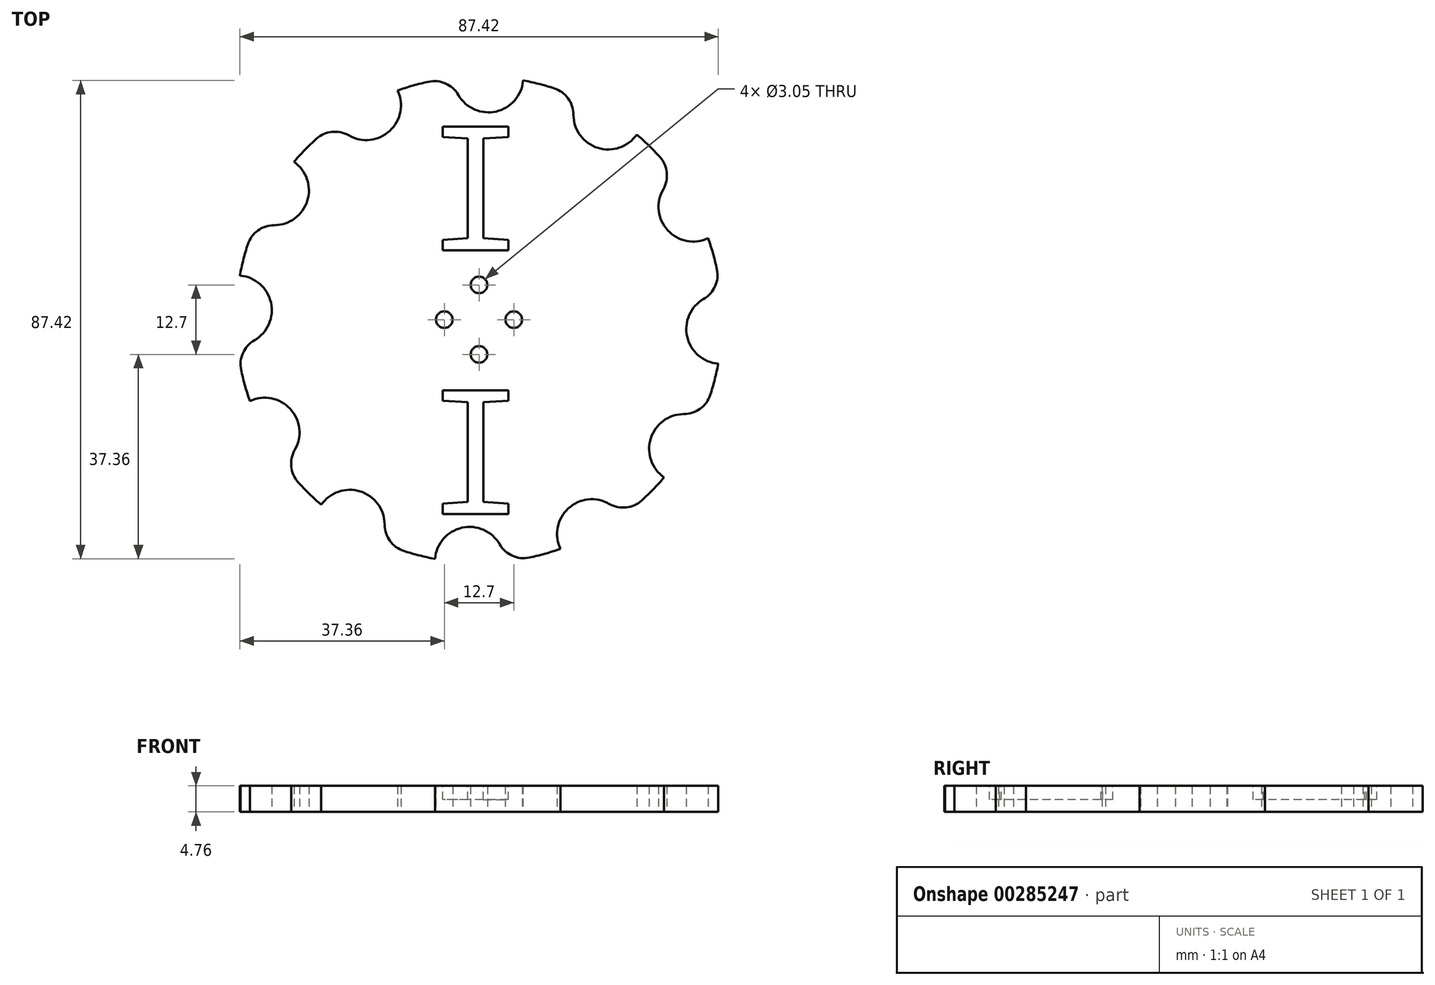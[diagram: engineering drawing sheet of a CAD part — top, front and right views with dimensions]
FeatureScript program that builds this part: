
annotation { "Feature Type Name" : "Feature", "Feature Type Description" : "" }
export const myFeature = defineFeature(function(context is Context, id is Id, definition is map)
    precondition{}
    {
        {
            var Q0;
            Q0=qCreatedBy(makeId("Top.planeOp"),FACE);
            var sketch = newSketch(context, id + "F0", { "sketchPlane" : qUnion([Q0])});
            skArc(sketch, "E0", {"start": v(-9.23, 43.48) * mm, "mid": v(-12.08, 42.78) * mm, "end": v(-14.88, 41.89) * mm});
            skCircle(sketch, "E1", {"center": v(0, 0) * mm, "radius": 6.35 * mm, "construction": true});
            skCircle(sketch, "E2", {"center": v(0, 6.35) * mm, "radius": 1.52 * mm});
            skCircle(sketch, "E3", {"center": v(-6.35, 0) * mm, "radius": 1.52 * mm});
            skCircle(sketch, "E4", {"center": v(0, -6.35) * mm, "radius": 1.52 * mm});
            skCircle(sketch, "E5", {"center": v(6.35, 0) * mm, "radius": 1.52 * mm});
            skArc(sketch, "E6", {"start": v(-3.77, 41.05) * mm, "mid": v(3.12, 38.03) * mm, "end": v(8.06, 43.71) * mm});
            skArc(sketch, "E7.1.0", {"start": v(-23.8, 33.67) * mm, "mid": v(-16.32, 34.5) * mm, "end": v(-14.88, 41.89) * mm});
            skArc(sketch, "E7.2.0", {"start": v(-37.44, 17.26) * mm, "mid": v(-31.38, 21.72) * mm, "end": v(-33.83, 28.83) * mm});
            skArc(sketch, "E7.3.0", {"start": v(-41.05, -3.77) * mm, "mid": v(-38.03, 3.12) * mm, "end": v(-43.71, 8.06) * mm});
            skArc(sketch, "E7.4.0", {"start": v(-33.67, -23.8) * mm, "mid": v(-34.5, -16.32) * mm, "end": v(-41.89, -14.88) * mm});
            skArc(sketch, "E7.5.0", {"start": v(-17.26, -37.44) * mm, "mid": v(-21.72, -31.38) * mm, "end": v(-28.83, -33.83) * mm});
            skArc(sketch, "E7.6.0", {"start": v(3.77, -41.05) * mm, "mid": v(-3.12, -38.03) * mm, "end": v(-8.06, -43.71) * mm});
            skArc(sketch, "E7.7.0", {"start": v(23.8, -33.67) * mm, "mid": v(16.32, -34.5) * mm, "end": v(14.88, -41.89) * mm});
            skArc(sketch, "E7.8.0", {"start": v(37.44, -17.26) * mm, "mid": v(31.38, -21.72) * mm, "end": v(33.83, -28.83) * mm});
            skArc(sketch, "E7.9.0", {"start": v(41.05, 3.77) * mm, "mid": v(38.03, -3.12) * mm, "end": v(43.71, -8.06) * mm});
            skArc(sketch, "E7.10.0", {"start": v(33.67, 23.8) * mm, "mid": v(34.5, 16.32) * mm, "end": v(41.89, 14.88) * mm});
            skArc(sketch, "E7.11.0", {"start": v(17.26, 37.44) * mm, "mid": v(21.72, 31.38) * mm, "end": v(28.83, 33.83) * mm});
            skArc(sketch, "E8.trimOffspring", {"start": v(13.75, 42.27) * mm, "mid": v(10.93, 43.09) * mm, "end": v(8.06, 43.71) * mm});
            skArc(sketch, "E9.trimOffspring", {"start": v(33.04, 29.73) * mm, "mid": v(31, 31.85) * mm, "end": v(28.83, 33.83) * mm});
            skArc(sketch, "E10.trimOffspring", {"start": v(43.48, 9.23) * mm, "mid": v(42.78, 12.08) * mm, "end": v(41.89, 14.88) * mm});
            skArc(sketch, "E11.trimOffspring", {"start": v(42.27, -13.75) * mm, "mid": v(43.09, -10.93) * mm, "end": v(43.71, -8.06) * mm});
            skArc(sketch, "E12.trimOffspring", {"start": v(29.73, -33.04) * mm, "mid": v(31.85, -31) * mm, "end": v(33.83, -28.83) * mm});
            skArc(sketch, "E13.trimOffspring", {"start": v(9.23, -43.48) * mm, "mid": v(12.08, -42.78) * mm, "end": v(14.88, -41.89) * mm});
            skArc(sketch, "E14.trimOffspring", {"start": v(-13.75, -42.27) * mm, "mid": v(-10.93, -43.09) * mm, "end": v(-8.06, -43.71) * mm});
            skArc(sketch, "E15.trimOffspring", {"start": v(-33.04, -29.73) * mm, "mid": v(-31, -31.85) * mm, "end": v(-28.83, -33.83) * mm});
            skArc(sketch, "E16.trimOffspring", {"start": v(-43.48, -9.23) * mm, "mid": v(-42.78, -12.08) * mm, "end": v(-41.89, -14.88) * mm});
            skArc(sketch, "E17.trimOffspring", {"start": v(-42.27, 13.75) * mm, "mid": v(-43.09, 10.93) * mm, "end": v(-43.71, 8.06) * mm});
            skArc(sketch, "E18.trimOffspring", {"start": v(-29.73, 33.04) * mm, "mid": v(-31.85, 31) * mm, "end": v(-33.83, 28.83) * mm});
            skPoint(sketch, "E19.visualSharp", {"position": v(-26.1, 35.97) * mm});
            skArc(sketch, "E19.filletArc", {"start": v(-23.8, 33.67) * mm, "mid": v(-26.86, 34.32) * mm, "end": v(-29.73, 33.04) * mm});
            skPoint(sketch, "E20.visualSharp", {"position": v(-40.6, 18.1) * mm});
            skArc(sketch, "E20.filletArc", {"start": v(-37.44, 17.26) * mm, "mid": v(-40.42, 16.29) * mm, "end": v(-42.27, 13.75) * mm});
            skPoint(sketch, "E21.visualSharp", {"position": v(-44.2, -4.62) * mm});
            skArc(sketch, "E21.filletArc", {"start": v(-41.05, -3.77) * mm, "mid": v(-43.15, -6.1) * mm, "end": v(-43.48, -9.23) * mm});
            skPoint(sketch, "E22.visualSharp", {"position": v(-35.97, -26.1) * mm});
            skArc(sketch, "E22.filletArc", {"start": v(-33.67, -23.8) * mm, "mid": v(-34.32, -26.86) * mm, "end": v(-33.04, -29.73) * mm});
            skPoint(sketch, "E23.visualSharp", {"position": v(-18.1, -40.6) * mm});
            skArc(sketch, "E23.filletArc", {"start": v(-17.26, -37.44) * mm, "mid": v(-16.29, -40.42) * mm, "end": v(-13.75, -42.27) * mm});
            skPoint(sketch, "E24.visualSharp", {"position": v(4.62, -44.2) * mm});
            skArc(sketch, "E24.filletArc", {"start": v(3.77, -41.05) * mm, "mid": v(6.1, -43.15) * mm, "end": v(9.23, -43.48) * mm});
            skPoint(sketch, "E25.visualSharp", {"position": v(26.1, -35.97) * mm});
            skArc(sketch, "E25.filletArc", {"start": v(23.8, -33.67) * mm, "mid": v(26.86, -34.32) * mm, "end": v(29.73, -33.04) * mm});
            skPoint(sketch, "E26.visualSharp", {"position": v(40.6, -18.1) * mm});
            skArc(sketch, "E26.filletArc", {"start": v(37.44, -17.26) * mm, "mid": v(40.42, -16.29) * mm, "end": v(42.27, -13.75) * mm});
            skPoint(sketch, "E27.visualSharp", {"position": v(44.2, 4.62) * mm});
            skArc(sketch, "E27.filletArc", {"start": v(41.05, 3.77) * mm, "mid": v(43.15, 6.1) * mm, "end": v(43.48, 9.23) * mm});
            skPoint(sketch, "E28.visualSharp", {"position": v(35.97, 26.1) * mm});
            skArc(sketch, "E28.filletArc", {"start": v(33.67, 23.8) * mm, "mid": v(34.32, 26.86) * mm, "end": v(33.04, 29.73) * mm});
            skPoint(sketch, "E29.visualSharp", {"position": v(18.1, 40.6) * mm});
            skArc(sketch, "E29.filletArc", {"start": v(17.26, 37.44) * mm, "mid": v(16.29, 40.42) * mm, "end": v(13.75, 42.27) * mm});
            skPoint(sketch, "E30.visualSharp", {"position": v(-4.62, 44.2) * mm});
            skArc(sketch, "E30.filletArc", {"start": v(-3.77, 41.05) * mm, "mid": v(-6.1, 43.15) * mm, "end": v(-9.23, 43.48) * mm});
            skSolve(sketch);
        }
        {
            var Q0;
            Q0=qSketchRegion(id+"F0",true);
            extrude(context, id + "F1", {"entities" : qUnion([Q0]), "depth" : 4.76 * mm});
        }
        {
            var Q0;
            Q0=makeQuery(id+"F1.opExtrude","CAP_FACE",FACE,{"disambiguationData":[OSD([sQuery(id+"F0.wireOp",EDGE,"E0"),sQuery(id+"F0.wireOp",EDGE,"E2"),sQuery(id+"F0.wireOp",EDGE,"E3"),sQuery(id+"F0.wireOp",EDGE,"E4"),sQuery(id+"F0.wireOp",EDGE,"E5"),sQuery(id+"F0.wireOp",EDGE,"E6"),sQuery(id+"F0.wireOp",EDGE,"E7.1.0"),sQuery(id+"F0.wireOp",EDGE,"E7.2.0"),sQuery(id+"F0.wireOp",EDGE,"E7.3.0"),sQuery(id+"F0.wireOp",EDGE,"E7.4.0"),sQuery(id+"F0.wireOp",EDGE,"E7.5.0"),sQuery(id+"F0.wireOp",EDGE,"E7.6.0"),sQuery(id+"F0.wireOp",EDGE,"E7.7.0"),sQuery(id+"F0.wireOp",EDGE,"E7.8.0"),sQuery(id+"F0.wireOp",EDGE,"E7.9.0"),sQuery(id+"F0.wireOp",EDGE,"E7.10.0"),sQuery(id+"F0.wireOp",EDGE,"E7.11.0"),sQuery(id+"F0.wireOp",EDGE,"E8.trimOffspring"),sQuery(id+"F0.wireOp",EDGE,"E9.trimOffspring"),sQuery(id+"F0.wireOp",EDGE,"E10.trimOffspring"),sQuery(id+"F0.wireOp",EDGE,"E11.trimOffspring"),sQuery(id+"F0.wireOp",EDGE,"E12.trimOffspring"),sQuery(id+"F0.wireOp",EDGE,"E13.trimOffspring"),sQuery(id+"F0.wireOp",EDGE,"E14.trimOffspring"),sQuery(id+"F0.wireOp",EDGE,"E15.trimOffspring"),sQuery(id+"F0.wireOp",EDGE,"E16.trimOffspring"),sQuery(id+"F0.wireOp",EDGE,"E17.trimOffspring"),sQuery(id+"F0.wireOp",EDGE,"E18.trimOffspring"),sQuery(id+"F0.wireOp",EDGE,"E19.filletArc"),sQuery(id+"F0.wireOp",EDGE,"E20.filletArc"),sQuery(id+"F0.wireOp",EDGE,"E21.filletArc"),sQuery(id+"F0.wireOp",EDGE,"E22.filletArc"),sQuery(id+"F0.wireOp",EDGE,"E23.filletArc"),sQuery(id+"F0.wireOp",EDGE,"E24.filletArc"),sQuery(id+"F0.wireOp",EDGE,"E25.filletArc"),sQuery(id+"F0.wireOp",EDGE,"E26.filletArc"),sQuery(id+"F0.wireOp",EDGE,"E27.filletArc"),sQuery(id+"F0.wireOp",EDGE,"E28.filletArc"),sQuery(id+"F0.wireOp",EDGE,"E29.filletArc"),sQuery(id+"F0.wireOp",EDGE,"E30.filletArc")])],"isStart":false});
            var sketch = newSketch(context, id + "F2", { "sketchPlane" : qUnion([Q0])});
            skText(sketch, "E31", { "text": "I", "fontName": "DroidSansMono.ttf"});
            const initialGuessF2  = {"E31": [-0.01012, 0.0127, 1, 0, 0.0228]};
            skSetInitialGuess(sketch, initialGuessF2);
            skSolve(sketch);
        }
        {
            var Q0;
            Q0=qSketchRegion(id+"F2",true);
            extrude(context, id + "F3", {"entities" : qUnion([Q0]), "operationType" : NewBodyOperationType.REMOVE, "oppositeDirection" : true, "depth" : 2.54 * mm});
        }
        {
            var Q0;
            Q0=makeQuery(id+"F1.opExtrude","CAP_FACE",FACE,{"disambiguationData":[OSD([sQuery(id+"F0.wireOp",EDGE,"E0"),sQuery(id+"F0.wireOp",EDGE,"E2"),sQuery(id+"F0.wireOp",EDGE,"E3"),sQuery(id+"F0.wireOp",EDGE,"E4"),sQuery(id+"F0.wireOp",EDGE,"E5"),sQuery(id+"F0.wireOp",EDGE,"E6"),sQuery(id+"F0.wireOp",EDGE,"E7.1.0"),sQuery(id+"F0.wireOp",EDGE,"E7.2.0"),sQuery(id+"F0.wireOp",EDGE,"E7.3.0"),sQuery(id+"F0.wireOp",EDGE,"E7.4.0"),sQuery(id+"F0.wireOp",EDGE,"E7.5.0"),sQuery(id+"F0.wireOp",EDGE,"E7.6.0"),sQuery(id+"F0.wireOp",EDGE,"E7.7.0"),sQuery(id+"F0.wireOp",EDGE,"E7.8.0"),sQuery(id+"F0.wireOp",EDGE,"E7.9.0"),sQuery(id+"F0.wireOp",EDGE,"E7.10.0"),sQuery(id+"F0.wireOp",EDGE,"E7.11.0"),sQuery(id+"F0.wireOp",EDGE,"E8.trimOffspring"),sQuery(id+"F0.wireOp",EDGE,"E9.trimOffspring"),sQuery(id+"F0.wireOp",EDGE,"E10.trimOffspring"),sQuery(id+"F0.wireOp",EDGE,"E11.trimOffspring"),sQuery(id+"F0.wireOp",EDGE,"E12.trimOffspring"),sQuery(id+"F0.wireOp",EDGE,"E13.trimOffspring"),sQuery(id+"F0.wireOp",EDGE,"E14.trimOffspring"),sQuery(id+"F0.wireOp",EDGE,"E15.trimOffspring"),sQuery(id+"F0.wireOp",EDGE,"E16.trimOffspring"),sQuery(id+"F0.wireOp",EDGE,"E17.trimOffspring"),sQuery(id+"F0.wireOp",EDGE,"E18.trimOffspring"),sQuery(id+"F0.wireOp",EDGE,"E19.filletArc"),sQuery(id+"F0.wireOp",EDGE,"E20.filletArc"),sQuery(id+"F0.wireOp",EDGE,"E21.filletArc"),sQuery(id+"F0.wireOp",EDGE,"E22.filletArc"),sQuery(id+"F0.wireOp",EDGE,"E23.filletArc"),sQuery(id+"F0.wireOp",EDGE,"E24.filletArc"),sQuery(id+"F0.wireOp",EDGE,"E25.filletArc"),sQuery(id+"F0.wireOp",EDGE,"E26.filletArc"),sQuery(id+"F0.wireOp",EDGE,"E27.filletArc"),sQuery(id+"F0.wireOp",EDGE,"E28.filletArc"),sQuery(id+"F0.wireOp",EDGE,"E29.filletArc"),sQuery(id+"F0.wireOp",EDGE,"E30.filletArc")])],"isStart":false});
            var sketch = newSketch(context, id + "F4", { "sketchPlane" : qUnion([Q0])});
            skSolve(sketch);
        }
        {
            var Q0;
            Q0=makeQuery(id+"F4.imprint","IMPRINT",FACE,{"disambiguationData":[TD([[makeQuery(id+"F4.imprint","IMPRINT",EDGE,{"derivedFrom":makeQuery(id+"F1.opExtrude","CAP_EDGE",EDGE,{"disambiguationData":[OSD([sQuery(id+"F0.wireOp",EDGE,"E0")])],"isStart":false})}),1.0]])]});
            var sketch = newSketch(context, id + "F5", { "sketchPlane" : qUnion([Q0])});
            skText(sketch, "E32", { "text": "I", "fontName": "DroidSansMono.ttf"});
            const initialGuessF5  = {"E32": [-0.01012, -0.0355, 1, 0, 0.0228]};
            skSetInitialGuess(sketch, initialGuessF5);
            skSolve(sketch);
        }
        {
            var Q0;
            Q0 = qSketchRegion(id + "F5", true);
            extrude(context, id + "F6", {"entities" : qUnion([Q0]), "operationType" : NewBodyOperationType.REMOVE, "oppositeDirection" : true, "depth" : 2.54 * mm});
        }
    });
